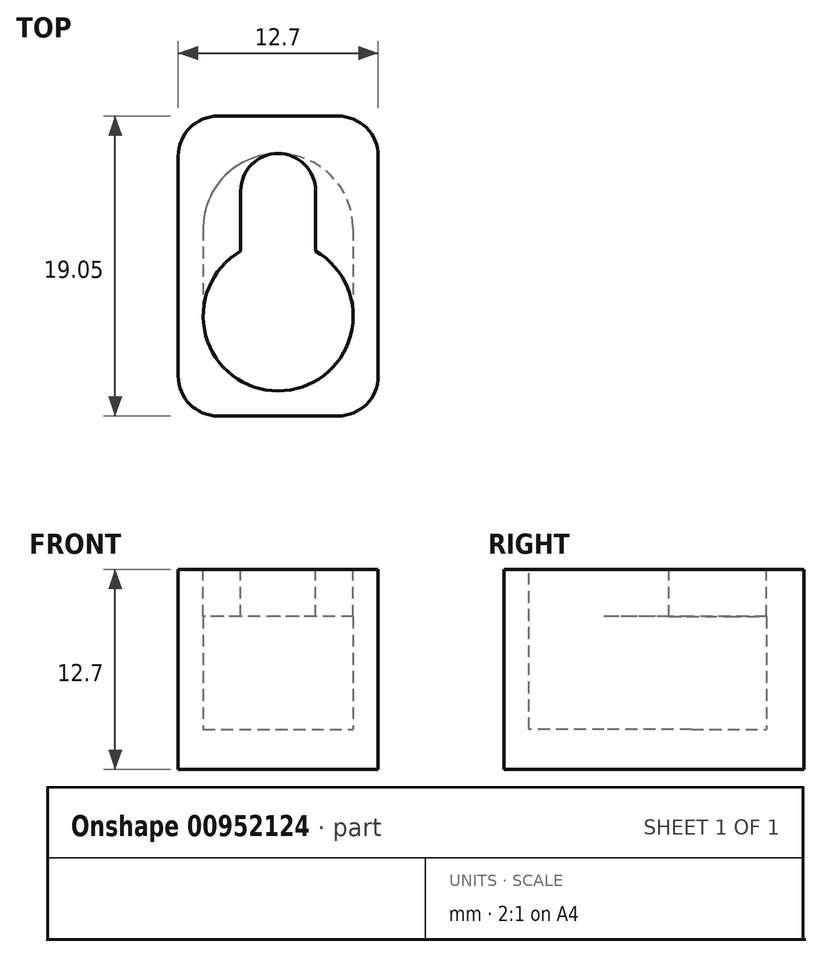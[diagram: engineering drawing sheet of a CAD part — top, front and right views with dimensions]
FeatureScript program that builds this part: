
annotation { "Feature Type Name" : "Feature", "Feature Type Description" : "" }
export const myFeature = defineFeature(function(context is Context, id is Id, definition is map)
    precondition{}
    {
        {
            var Q0;
            Q0=qCreatedBy(makeId("Top.planeOp"),FACE);
            var sketch = newSketch(context, id + "F0", { "sketchPlane" : qUnion([Q0])});
            skLineSegment(sketch, "E0.bottom", {"start": v(0, 0) * mm, "end": v(12.7, 0) * mm});
            skLineSegment(sketch, "E0.top", {"start": v(0, 19.05) * mm, "end": v(12.7, 19.05) * mm});
            skLineSegment(sketch, "E0.left", {"start": v(0, 0) * mm, "end": v(0, 19.05) * mm});
            skLineSegment(sketch, "E0.right", {"start": v(12.7, 0) * mm, "end": v(12.7, 19.05) * mm});
            skSolve(sketch);
        }
        {
            var Q0;
            Q0=makeQuery(id+"F0.imprint","IMPRINT",FACE,{"disambiguationData":[TD([[makeQuery(id+"F0.imprint","IMPRINT",EDGE,{"derivedFrom":sQuery(id+"F0.wireOp",EDGE,"E0.bottom")}),1.0]])]});
            extrude(context, id + "F1", {"entities" : qUnion([Q0]), "depth" : 12.7 * mm, "offsetDistance" : 25.4 * mm});
        }
        {
            var Q0;
            Q0=makeQuery(id+"F1.opExtrude","CAP_FACE",FACE,{"disambiguationData":[OSD([sQuery(id+"F0.wireOp",EDGE,"E0.bottom"),sQuery(id+"F0.wireOp",EDGE,"E0.top"),sQuery(id+"F0.wireOp",EDGE,"E0.left"),sQuery(id+"F0.wireOp",EDGE,"E0.right")])],"isStart":false});
            var sketch = newSketch(context, id + "F2", { "sketchPlane" : qUnion([Q0])});
            skArc(sketch, "E1", {"start": v(3.97, 10.47) * mm, "mid": v(6.35, 1.59) * mm, "end": v(8.73, 10.47) * mm});
            skArc(sketch, "E2", {"start": v(8.73, 14.29) * mm, "mid": v(6.35, 16.67) * mm, "end": v(3.97, 14.29) * mm});
            skLineSegment(sketch, "E3", {"start": v(3.97, 14.29) * mm, "end": v(3.97, 10.47) * mm});
            skLineSegment(sketch, "E4", {"start": v(8.73, 14.29) * mm, "end": v(8.73, 10.47) * mm});
            skSolve(sketch);
        }
        {
            var Q0;
            Q0=makeQuery(id+"F2.imprint","IMPRINT",FACE,{"disambiguationData":[TD([[makeQuery(id+"F2.imprint","IMPRINT",EDGE,{"derivedFrom":sQuery(id+"F2.wireOp",EDGE,"E1")}),1.0]])]});
            extrude(context, id + "F3", {"entities" : qUnion([Q0]), "operationType" : NewBodyOperationType.REMOVE, "oppositeDirection" : true, "depth" : 10.16 * mm, "offsetDistance" : 25.4 * mm});
        }
        {
            var Q0;
            Q0=makeQuery(id+"F3.boolean.opBoolean","COPY",FACE,{"derivedFrom":makeQuery(id+"F3.opExtrude","CAP_FACE",FACE,{"disambiguationData":[OSD([sQuery(id+"F2.wireOp",EDGE,"E1"),sQuery(id+"F2.wireOp",EDGE,"E2"),sQuery(id+"F2.wireOp",EDGE,"E3"),sQuery(id+"F2.wireOp",EDGE,"E4")])],"isStart":false})});
            var sketch = newSketch(context, id + "F4", { "sketchPlane" : qUnion([Q0])});
            skArc(sketch, "E5.0", {"start": v(1.59, 6.35) * mm, "mid": v(6.35, 1.59) * mm, "end": v(11.11, 6.35) * mm});
            skArc(sketch, "E6.0", {"start": v(8.73, 14.29) * mm, "mid": v(6.35, 16.67) * mm, "end": v(3.97, 14.29) * mm, "construction": true});
            skArc(sketch, "E7", {"start": v(11.11, 11.9) * mm, "mid": v(6.35, 16.67) * mm, "end": v(1.59, 11.9) * mm});
            skLineSegment(sketch, "E8", {"start": v(1.59, 11.9) * mm, "end": v(1.59, 6.35) * mm});
            skLineSegment(sketch, "E9", {"start": v(11.11, 11.9) * mm, "end": v(11.11, 6.35) * mm});
            skPoint(sketch, "E10.orphan", {"position": v(3.97, 10.47) * mm});
            skPoint(sketch, "E11.orphan", {"position": v(8.73, 10.47) * mm});
            skSolve(sketch);
        }
        {
            var Q0;
            Q0 = qSketchRegion(id + "F4", true);
            extrude(context, id + "F5", {"entities" : qUnion([Q0]), "operationType" : NewBodyOperationType.REMOVE, "depth" : 7.16 * mm, "offsetDistance" : 25.4 * mm});
        }
        {
            var Q0;
            Q0=makeQuery(id+"F1.opExtrude","SWEPT_EDGE",EDGE,{"disambiguationData":[OSD([sQuery(id+"F0.wireOp",EDGE,"E0.bottom"),sQuery(id+"F0.wireOp",EDGE,"E0.right")])]});
            var Q1;
            Q1=makeQuery(id+"F1.opExtrude","SWEPT_EDGE",EDGE,{"disambiguationData":[OSD([sQuery(id+"F0.wireOp",EDGE,"E0.top"),sQuery(id+"F0.wireOp",EDGE,"E0.right")])]});
            var Q2;
            Q2=makeQuery(id+"F1.opExtrude","SWEPT_EDGE",EDGE,{"disambiguationData":[OSD([sQuery(id+"F0.wireOp",EDGE,"E0.bottom"),sQuery(id+"F0.wireOp",EDGE,"E0.left")])]});
            var Q3;
            Q3=makeQuery(id+"F1.opExtrude","SWEPT_EDGE",EDGE,{"disambiguationData":[OSD([sQuery(id+"F0.wireOp",EDGE,"E0.top"),sQuery(id+"F0.wireOp",EDGE,"E0.left")])]});
            fillet(context, id + "F6", {"entities" : qUnion([Q0, Q1, Q2, Q3]), "radius" : 2.54 * mm, "tangentPropagation" : true, "allowEdgeOverflow" : false});
        }
    });
